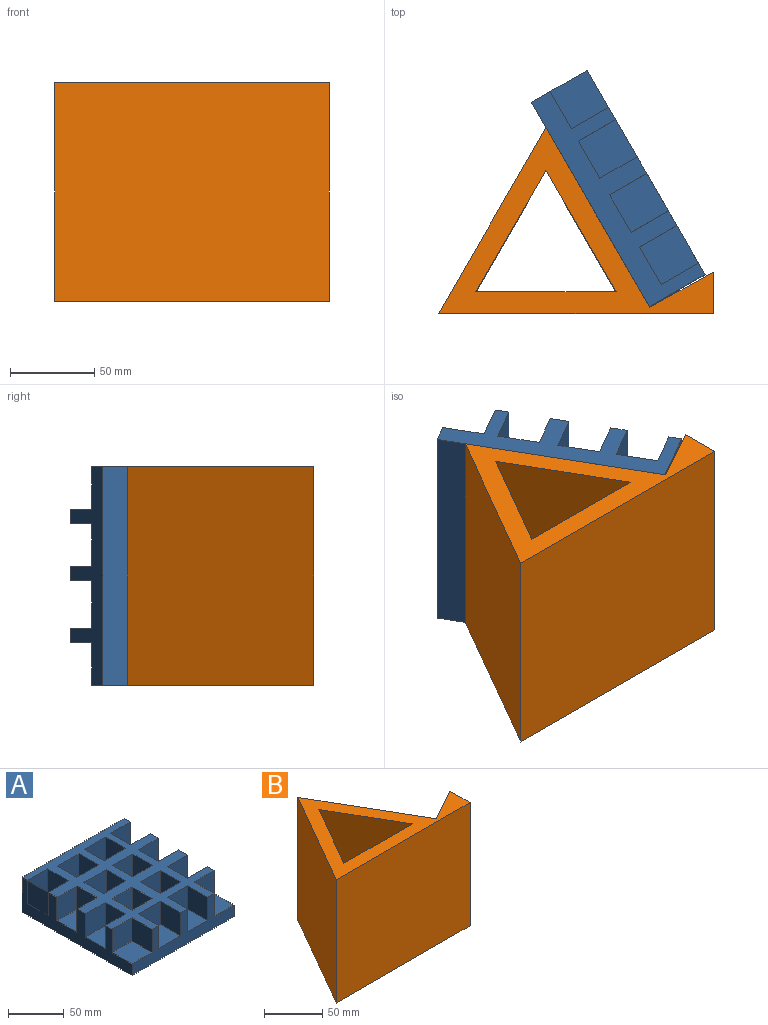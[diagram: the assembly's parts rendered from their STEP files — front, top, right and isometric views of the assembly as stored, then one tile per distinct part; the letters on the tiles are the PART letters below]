
ASSEMBLY  parts=2 mates=1
PART A: 75 faces, bbox 129.5x139.7x38.1 mm
  f0: plane 129.54x38.1mm, normal (0,-1,0), area 2283.9mm2, adj f1,f2,f4,f5,f6,f7,f29,f31
  f1: plane 139.7x38.1mm, normal (1,0,0), area 2734mm2, adj f0,f2,f3,f5,f9,f10,f27,f28
  f2: plane 139.7x129.54mm, normal (0,0,1), area 7597.6mm2, adj f0,f1,f3,f4,f6,f7,f8,f9
  f3: plane 129.54x38.1mm, normal (0,1,0), area 4935.5mm2, adj f1,f2,f4,f5
  f4: plane 139.7x38.1mm, normal (-1,0,0), area 3387.1mm2, adj f0,f2,f3,f5,f20,f22,f23,f25
  f5: plane 139.7x129.54mm, normal (0,0,-1), area 18096.7mm2, adj f0,f1,f3,f4
  f6: plane 25.4x25.4mm, normal (1,0,0), area 645.2mm2, adj f0,f2,f8,f64
  f7: plane 25.4x25.4mm, normal (-1,0,0), area 645.2mm2, adj f0,f2,f8,f64
  f8: plane 28.19x25.4mm, normal (0,-1,0), area 716.1mm2, adj f2,f6,f7,f64
  f9: plane 25.4x24.74mm, normal (0,1,0), area 628.4mm2, adj f1,f2,f11,f61
  f10: plane 25.4x24.74mm, normal (0,-1,0), area 628.4mm2, adj f1,f2,f11,f61
  f11: plane 25.56x25.4mm, normal (1,0,0), area 649.1mm2, adj f2,f9,f10,f61
  f12: plane 25.4x25.4mm, normal (1,0,0), area 645.2mm2, adj f2,f13,f15,f74
  f13: plane 25.4x25.29mm, normal (0,1,0), area 642.4mm2, adj f2,f12,f14,f74
  f14: plane 25.4x24.73mm, normal (-1,0,0), area 628.2mm2, adj f2,f13,f15,f74
  f15: plane 25.4x25.29mm, normal (-0.03,-1,0), area 642.6mm2, adj f2,f12,f14,f74
  f16: plane 25.4x24.76mm, normal (1,0,0), area 628.9mm2, adj f2,f17,f19,f73
  f17: plane 27.08x25.4mm, normal (0,1,0), area 687.8mm2, adj f2,f16,f18,f73
  f18: plane 25.4x24.76mm, normal (-1,0,0), area 628.9mm2, adj f2,f17,f19,f73
  f19: plane 27.08x25.4mm, normal (0,-1,0), area 687.8mm2, adj f2,f16,f18,f73
  f20: plane 25.4x25.4mm, normal (0,1,0), area 645.2mm2, adj f2,f4,f21,f60
  f21: plane 25.4x25.4mm, normal (-1,0,0), area 645.2mm2, adj f2,f20,f22,f60
  f22: plane 25.4x25.4mm, normal (0,-1,0), area 645.2mm2, adj f2,f4,f21,f60
  f23: plane 25.4x25.4mm, normal (0,1,0), area 645.2mm2, adj f2,f4,f24,f59
  f24: plane 25.4x25.4mm, normal (-1,0,0), area 645.2mm2, adj f2,f23,f25,f59
  f25: plane 25.4x25.4mm, normal (0,-1,0), area 645.2mm2, adj f2,f4,f24,f59
  f26: plane 25.4x25.4mm, normal (1,0,0), area 645.2mm2, adj f2,f27,f28,f62
  f27: plane 25.4x25.4mm, normal (0,1,0), area 645.2mm2, adj f1,f2,f26,f62
  f28: plane 25.4x25.4mm, normal (0.01,-1,0), area 645.2mm2, adj f1,f2,f26,f62
  f29: plane 25.4x25.4mm, normal (-1,0,0), area 645.2mm2, adj f0,f2,f30,f65
  f30: plane 25.4x25.4mm, normal (0,-1,0), area 645.2mm2, adj f2,f29,f31,f65
  f31: plane 25.4x25.4mm, normal (1,0,0), area 645.2mm2, adj f0,f2,f30,f65
  f32: plane 25.4x25.4mm, normal (1,0,0), area 645.2mm2, adj f2,f33,f35,f72
  f33: plane 25.4x25.4mm, normal (0,1,0), area 645.2mm2, adj f2,f32,f34,f72
  f34: plane 25.4x25.4mm, normal (-1,0,0), area 645.2mm2, adj f2,f33,f35,f72
  f35: plane 25.4x25.4mm, normal (0,-1,0), area 645.2mm2, adj f2,f32,f34,f72
  f36: plane 25.4x25.4mm, normal (1,0,0), area 645.2mm2, adj f2,f37,f39,f71
  f37: plane 25.4x25.4mm, normal (0,1,0), area 645.2mm2, adj f2,f36,f38,f71
  f38: plane 25.4x25.4mm, normal (-1,0,0), area 645.2mm2, adj f2,f37,f39,f71
  f39: plane 25.4x25.4mm, normal (0,-1,0), area 645.2mm2, adj f2,f36,f38,f71
  f40: plane 25.4x25.4mm, normal (0,-1,0), area 645.2mm2, adj f1,f2,f41,f63
  f41: plane 25.4x25.4mm, normal (1,0,0), area 645.2mm2, adj f2,f40,f42,f63
  f42: plane 25.4x25.4mm, normal (0,1,0), area 645.2mm2, adj f1,f2,f41,f63
  f43: plane 25.4x24.97mm, normal (-1,0,0), area 634.2mm2, adj f2,f44,f46,f70
  f44: plane 28.28x25.4mm, normal (0,-1,0), area 718.3mm2, adj f2,f43,f45,f70
  f45: plane 25.4x24.97mm, normal (1,0,0), area 634.2mm2, adj f2,f44,f46,f70
  f46: plane 28.28x25.4mm, normal (0,1,0), area 718.3mm2, adj f2,f43,f45,f70
  f47: plane 25.56x25.4mm, normal (0,1,0), area 649.1mm2, adj f2,f48,f50,f69
  f48: plane 26.09x25.4mm, normal (-1,0,0), area 662.7mm2, adj f2,f47,f49,f69
  f49: plane 25.56x25.4mm, normal (0,-1,0), area 649.1mm2, adj f2,f48,f50,f69
  f50: plane 26.09x25.4mm, normal (1,0,0), area 662.7mm2, adj f2,f47,f49,f69
  f51: plane 27.15x25.4mm, normal (0,-1,0), area 689.7mm2, adj f2,f52,f54,f68
  f52: plane 25.4x24.49mm, normal (1,0,0), area 622.1mm2, adj f2,f51,f53,f68
  f53: plane 27.15x25.4mm, normal (0,1,0), area 689.7mm2, adj f2,f52,f54,f68
  f54: plane 25.4x24.49mm, normal (-1,0,0), area 622.1mm2, adj f2,f51,f53,f68
  f55: plane 25.4x25.4mm, normal (0,-1,0), area 645.2mm2, adj f2,f4,f56,f67
  f56: plane 25.4x25.4mm, normal (-1,0,0), area 645.2mm2, adj f0,f2,f55,f67
  f57: plane 25.4x25.4mm, normal (0,-1,0), area 645.2mm2, adj f1,f2,f58,f66
  f58: plane 25.4x25.4mm, normal (1,0,0), area 645.2mm2, adj f0,f2,f57,f66
  f59: plane 25.4x25.4mm, normal (0,0,1), area 645.2mm2, adj f4,f23,f24,f25
  f60: plane 25.4x25.4mm, normal (0,0,1), area 645.2mm2, adj f4,f20,f21,f22
  f61: plane 25.56x24.74mm, normal (0,0,1), area 632.2mm2, adj f1,f9,f10,f11
  f62: plane 25.56x25.4mm, normal (0,0,1), area 647.2mm2, adj f1,f26,f27,f28
  f63: plane 25.4x25.4mm, normal (0,0,1), area 645.2mm2, adj f1,f40,f41,f42
  f64: plane 28.19x25.4mm, normal (0,0,1), area 716.1mm2, adj f0,f6,f7,f8
  f65: plane 25.4x25.4mm, normal (0,0,1), area 645.2mm2, adj f0,f29,f30,f31
  f66: plane 25.4x25.4mm, normal (0,0,1), area 645.2mm2, adj f0,f1,f57,f58
  f67: plane 25.4x25.4mm, normal (0,0,1), area 645.2mm2, adj f0,f4,f55,f56
  f68: plane 27.15x24.49mm, normal (0,0,1), area 665.1mm2, adj f51,f52,f53,f54
  f69: plane 26.09x25.56mm, normal (0,0,1), area 666.8mm2, adj f47,f48,f49,f50
  f70: plane 28.28x24.97mm, normal (0,0,1), area 706.1mm2, adj f43,f44,f45,f46
  f71: plane 25.4x25.4mm, normal (0,0,1), area 645.2mm2, adj f36,f37,f38,f39
  f72: plane 25.4x25.4mm, normal (0,0,1), area 645.2mm2, adj f32,f33,f34,f35
  f73: plane 27.08x24.76mm, normal (0,0,1), area 670.4mm2, adj f16,f17,f18,f19
  f74: plane 25.4x25.29mm, normal (0,0,1), area 633.9mm2, adj f12,f13,f14,f15
PART B: 10 faces, bbox 162.6x110x129.5 mm
  f0: plane 129.54x106.46mm, normal (0.87,0.5,0), area 15924.2mm2, adj f1,f4,f5,f6
  f1: plane 129.54x109.99mm, normal (-0.87,0.5,0), area 16451.6mm2, adj f0,f2,f5,f6
  f2: plane 162.56x129.54mm, normal (0,-1,0), area 21058mm2, adj f1,f3,f5,f6
  f3: plane 129.54x24.44mm, normal (1,0,0), area 3166.1mm2, adj f2,f4,f5,f6
  f4: plane 129.54x37.6mm, normal (-0.49,0.87,0), area 5573.1mm2, adj f0,f3,f5,f6
  f5: plane 162.56x109.99mm, normal (0,0,1), area 4522.8mm2, adj f0,f1,f2,f3,f4,f7,f8,f9
  f6: plane 162.56x109.99mm, normal (0,0,-1), area 4522.8mm2, adj f0,f1,f2,f3,f4,f7,f8,f9
  f7: plane 129.54x71.89mm, normal (-0.87,-0.5,0), area 10752.6mm2, adj f5,f6,f8,f9
  f8: plane 129.54x71.89mm, normal (0.87,-0.5,0), area 10752.6mm2, adj f5,f6,f7,f9
  f9: plane 129.54x83.01mm, normal (0,1,0), area 10752.6mm2, adj f5,f6,f7,f8
PLACE A rot(axis=(-0.69,-0.19,-0.69),158.9deg) t=(53.73,75.93,12.23)mm
PLACE B t=(-30.33,40.45,-52.54)mm
MATE fastened A.f5 <-> B.f0  axis (-0.87,-0.5,0) through (53.73,75.93,12.23)mm
